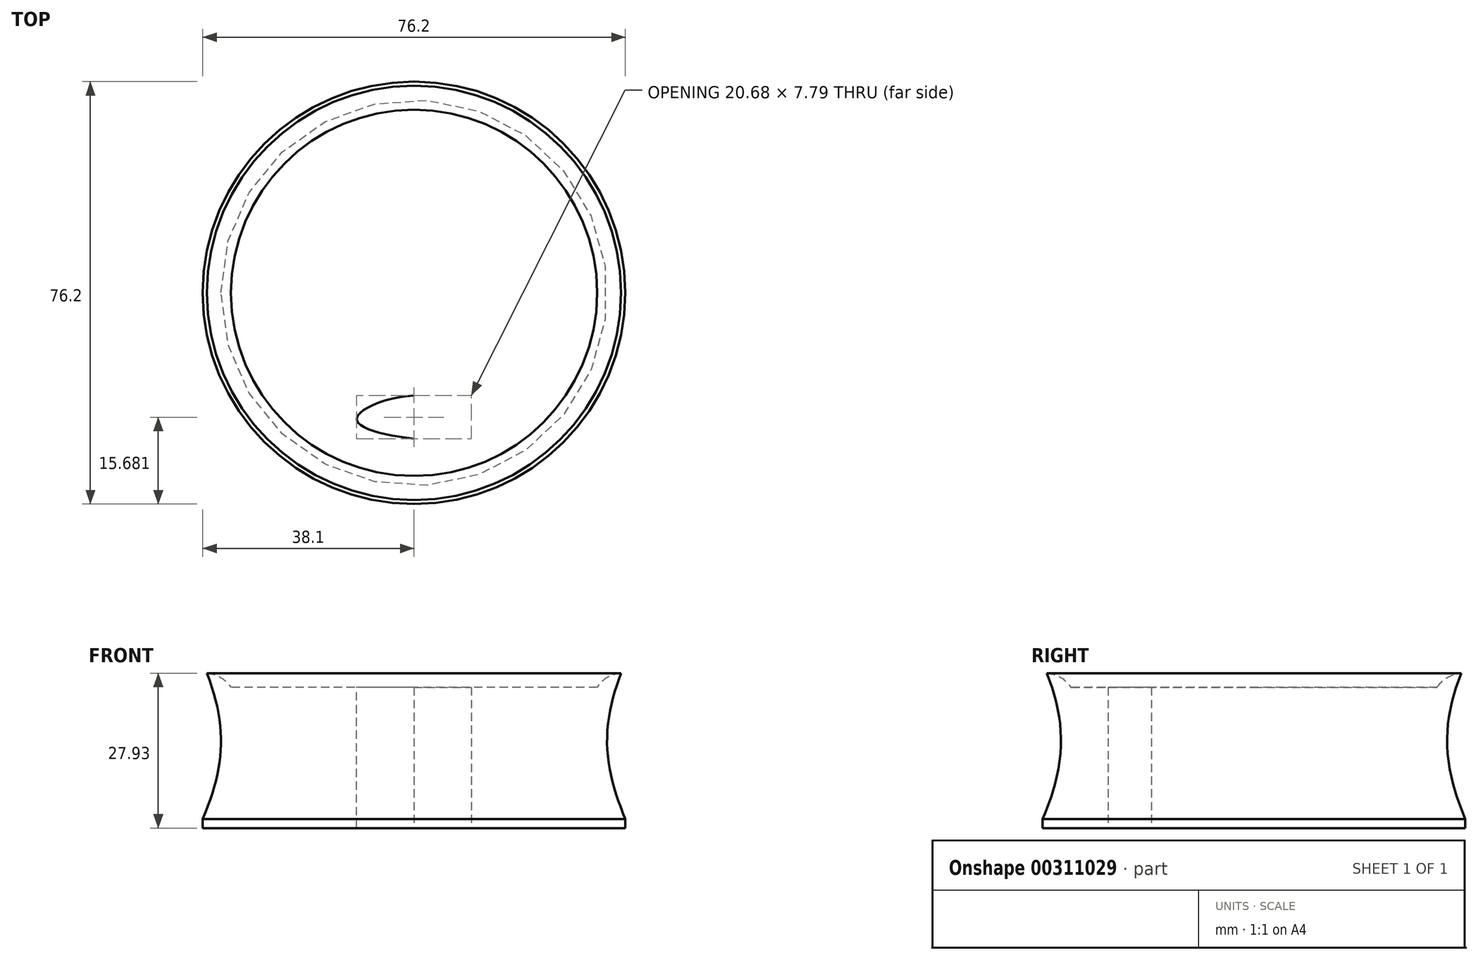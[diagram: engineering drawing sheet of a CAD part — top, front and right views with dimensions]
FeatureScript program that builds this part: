
annotation { "Feature Type Name" : "Feature", "Feature Type Description" : "" }
export const myFeature = defineFeature(function(context is Context, id is Id, definition is map)
    precondition{}
    {
        {
            var Q0;
            Q0=qCreatedBy(makeId("Top.planeOp"),FACE);
            var sketch = newSketch(context, id + "F0", { "sketchPlane" : qUnion([Q0])});
            skCircle(sketch, "E0", {"center": v(0, 0) * mm, "radius": 33.02 * mm});
            skCircle(sketch, "E1", {"center": v(0, 0) * mm, "radius": 38.1 * mm});
            skLineSegment(sketch, "E2", {"start": v(0, 69.27) * mm, "end": v(0, -54.23) * mm, "construction": true});
            skLineSegment(sketch, "E3", {"start": v(-69.67, 0) * mm, "end": v(68.87, 0) * mm, "construction": true});
            skFitSpline(sketch, "E4", {"points": [v(0, -18.53) * mm, v(-10.34, -22.82) * mm, v(0, -26.31) * mm], "startDerivative": vector(-31.21, -1.6) * mm, "endDerivative": vector(30, -3.24) * mm});
            skFitSpline(sketch, "E5.MirrorCS", {"points": [v(0, -18.53) * mm, v(10.34, -22.82) * mm, v(0, -26.31) * mm], "startDerivative": vector(31.21, -1.6) * mm, "endDerivative": vector(-30, -3.24) * mm});
            skSolve(sketch);
        }
        {
            var Q0;
            Q0=makeQuery(id+"F0.imprint","IMPRINT",FACE,{"disambiguationData":[TD([[makeQuery(id+"F0.imprint","IMPRINT",EDGE,{"derivedFrom":sQuery(id+"F0.wireOp",EDGE,"E0")}),-1.0]])]});
            extrude(context, id + "F1", {"entities" : qUnion([Q0]), "depth" : 27.94 * mm});
        }
        {
            var Q0;
            Q0=makeQuery(id+"F0.imprint","IMPRINT",FACE,{"disambiguationData":[TD([[makeQuery(id+"F0.imprint","IMPRINT",EDGE,{"derivedFrom":sQuery(id+"F0.wireOp",EDGE,"E0")}),1.0]])]});
            extrude(context, id + "F2", {"entities" : qUnion([Q0]), "operationType" : NewBodyOperationType.ADD, "depth" : 25.4 * mm});
        }
        {
            var Q0;
            Q0=makeQuery(id+"F1.opExtrude","CAP_EDGE",EDGE,{"disambiguationData":[OSD([sQuery(id+"F0.wireOp",EDGE,"E0")])],"isStart":false});
            fillet(context, id + "F3", {"entities" : qUnion([Q0]), "radius" : 5.6 * mm, "tangentPropagation" : true, "allowEdgeOverflow" : false});
        }
        {
            var Q0;
            Q0=qCreatedBy(makeId("Front.planeOp"),FACE);
            var sketch = newSketch(context, id + "F4", { "sketchPlane" : qUnion([Q0])});
            skLineSegment(sketch, "E6", {"start": v(0, 56.38) * mm, "end": v(0, -43.23) * mm, "construction": true});
            skFitSpline(sketch, "E7", {"points": [v(38.39, 30.43) * mm, v(38.8, 0) * mm], "startDerivative": vector(-15.7, -35.72) * mm, "endDerivative": vector(14.5, -33.02) * mm});
            skLineSegment(sketch, "E8", {"start": v(38.39, 30.43) * mm, "end": v(38.8, 0) * mm});
            skSolve(sketch);
        }
        {
            var Q0;
            Q0=makeQuery(id+"F4.imprint","IMPRINT",FACE,{"disambiguationData":[TD([[makeQuery(id+"F4.imprint","IMPRINT",EDGE,{"derivedFrom":sQuery(id+"F4.wireOp",EDGE,"E7")}),1.0]])]});
            var Q1;
            Q1=sQuery(id+"F4.wireOp",EDGE,"E6");
            revolve(context, id + "F5", {"operationType" : NewBodyOperationType.REMOVE, "entities" : qUnion([Q0]), "axis" : qUnion([Q1]), "revolveType" : RevolveType.FULL, "oppositeDirection" : true});
        }
    });
